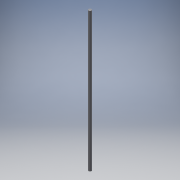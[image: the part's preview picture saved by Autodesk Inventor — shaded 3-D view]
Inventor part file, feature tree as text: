
AUTODESK INVENTOR PART (.ipt)
format: ipt  version: 2019 (Build 230136000, 136)  size: 88,576 bytes
history: native  units: in
note: dims shown in document units (in); Inventor stores cm internally (conversion verified against a paired STEP export)
features: extrude x1, sketch x1
ambient origin geometry x8: Origin, YZ Plane, XZ Plane, XY Plane, X Axis, Y Axis, Z Axis, Center Point
bodies: Solid1 (feature_tree)
feature tree (2):
  extrude  "Extrusion1"  Depth=14.5472in TaperAngle=0.0deg
  sketch  "Sketch1"  dims[d0=0.315in d1=14.5472in d2=0.0in]
